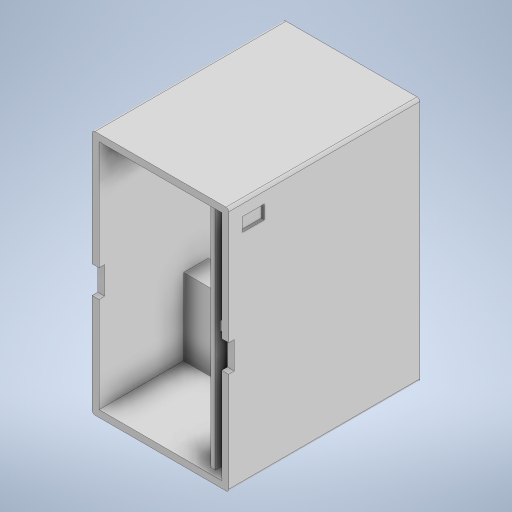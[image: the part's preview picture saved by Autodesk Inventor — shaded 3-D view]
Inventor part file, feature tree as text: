
AUTODESK INVENTOR PART (.ipt)
format: ipt  version: 2023.1 (Build 271208000, 208)  size: 420,864 bytes
history: native  units: mm
features: extrude x15, sketch x14, projected_geometry x5, thread x2, plane x1, fillet x1
ambient origin geometry x8: Origin, YZ Plane, XZ Plane, XY Plane, X Axis, Y Axis, Z Axis, Center Point
bodies: 实体1 (feature_tree)
feature tree (38):
  extrude  "拉伸1"  Depth=900.0mm
  extrude  "拉伸2"  Depth=850.0mm
  extrude  "拉伸3"  Depth=675.0mm TaperAngle=0.0deg
  plane  "工作平面1"
  extrude  "拉伸4"  TaperAngle=0.0deg  [1 undecoded]
  extrude  "拉伸7"  Depth=60.0mm
  extrude  "拉伸8"  Depth=25.0mm TaperAngle=0.0deg
  extrude  "拉伸5"  Depth=25.0mm
  extrude  "拉伸6"  Depth=20.0mm
  thread  "螺纹1"  [1 undecoded]
  thread  "螺纹2"  [1 undecoded]
  fillet  "圆角1"  Radius=25.0mm
  extrude  "拉伸10"  Depth=45.0mm
  extrude  "拉伸11"  Depth=850.0mm
  extrude  "拉伸13"  Depth=390.0mm
  extrude  "拉伸15"  Depth=300.0mm
  extrude  "拉伸16"  Depth=390.0mm
  extrude  "拉伸17"  Depth=80.0mm
  extrude  "拉伸19"  Depth=20.0mm
  sketch  "草图1"  dims[d0=500.0mm d1=900.0mm]
  sketch  "草图2"  dims[d2=700.0mm d3=0.0mm d4=850.0mm]
  sketch  "草图3"  dims[d5=450.0mm d6=675.0mm d7=0.0mm]
  sketch  "草图4"  dims[d8=250.0mm d9=0.0mm d10=0.0mm]
  sketch  "草图6"  dims[d12=0.0mm d13=0.0mm d14=60.0mm]
  sketch  "草图7"  dims[d15=30.0mm d16=25.0mm d17=0.0mm]
  projected_geometry  "投影回路1"
  projected_geometry  "投影回路2"
  sketch  "草图12"  dims[d18=25.0mm d19=0.0mm d20=12.0mm]
  sketch  "草图14"  dims[d21=12.0mm d22=20.0mm d23=25.0mm d24=25.0mm d25=0.0mm d26=25.0mm d27=0.0mm]
  sketch  "草图15"  dims[d28=10.0mm d30=45.0mm]
  projected_geometry  "投影回路3"
  sketch  "草图17"  dims[d31=15.0mm d32=0.0mm d33=850.0mm]
  sketch  "草图19"  dims[d35=390.0mm d38=390.0mm]
  sketch  "草图20"  dims[d40=90.0mm d41=300.0mm]
  projected_geometry  "投影回路4"
  sketch  "草图23"  dims[d42=280.0mm d60=390.0mm]
  projected_geometry  "投影回路5"
  sketch  "草图25"  dims[d61=15.0mm d62=0.0mm d69=80.0mm d70=20.0mm d72=10.0mm d73=0.0mm d74=40.0mm d76=10.0mm d77=0.0mm d83=480.0mm d84=55.0mm d85=225.0mm d86=130.0mm d87=120.0mm d88=120.0mm d89=10.0mm d90=0.0mm d93=80.0mm d94=50.0mm d95=50.0mm d96=50.0mm d97=10.0mm d98=0.0mm d99=5.0mm d100=30.0mm d101=10.0mm d102=0.0mm d107=10.0mm d108=0.0mm d110=20.0mm d111=200.0mm d112=80.0mm d115=20.0mm d117=20.0mm d118=405.0mm d120=20.0mm d121=100.0mm d122=0.0mm d123=0.0mm d124=365.0mm d66=0.5mm d67=0.872665mm d68=0.5mm]
note: 3 required parameter values undecoded (feature->parameter linkage not recoverable at this tier; creation-order binding heuristic only, values carry confidence <= 0.55)
